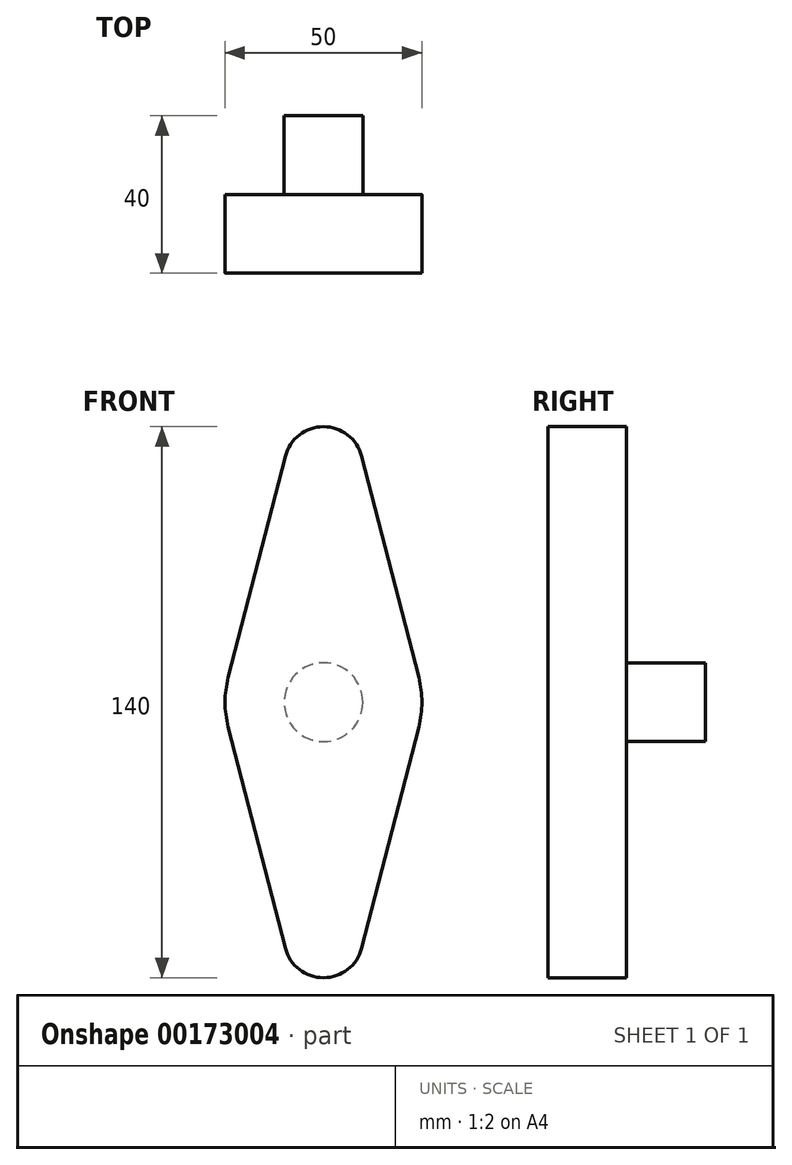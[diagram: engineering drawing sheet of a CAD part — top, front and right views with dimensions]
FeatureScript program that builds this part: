
annotation { "Feature Type Name" : "Feature", "Feature Type Description" : "" }
export const myFeature = defineFeature(function(context is Context, id is Id, definition is map)
    precondition{}
    {
        {
            var Q0;
            Q0=qCreatedBy(makeId("Front.planeOp"),FACE);
            var sketch = newSketch(context, id + "F0", { "sketchPlane" : qUnion([Q0])});
            skCircle(sketch, "E0", {"center": v(0, 0) * mm, "radius": 25 * mm});
            skCircle(sketch, "E1", {"center": v(0, 60) * mm, "radius": 10 * mm});
            skCircle(sketch, "E2", {"center": v(0, -60) * mm, "radius": 10 * mm});
            skLineSegment(sketch, "E3", {"start": v(0, 0) * mm, "end": v(0, 60) * mm, "construction": true});
            skLineSegment(sketch, "E4", {"start": v(0, 0) * mm, "end": v(0, -60) * mm, "construction": true});
            skLineSegment(sketch, "E5", {"start": v(-9.68, 62.5) * mm, "end": v(-24.2, 6.25) * mm});
            skLineSegment(sketch, "E6.MirrorCS", {"start": v(9.68, 62.5) * mm, "end": v(24.2, 6.25) * mm});
            skLineSegment(sketch, "E7", {"start": v(-24.2, -6.25) * mm, "end": v(-9.68, -62.5) * mm});
            skLineSegment(sketch, "E8.MirrorCS", {"start": v(24.2, -6.25) * mm, "end": v(9.68, -62.5) * mm});
            skSolve(sketch);
        }
        {
            var Q0;
            Q0 = qSketchRegion(id + "F0", true);
            extrude(context, id + "F1", {"entities" : qUnion([Q0]), "depth" : 20 * mm});
        }
        {
            var Q0;
            Q0=makeQuery(id+"F1.opExtrude","CAP_FACE",FACE,{"disambiguationData":[OSD([sQuery(id+"F0.wireOp",EDGE,"E0"),sQuery(id+"F0.wireOp",EDGE,"E1"),sQuery(id+"F0.wireOp",EDGE,"E2"),sQuery(id+"F0.wireOp",EDGE,"E5"),sQuery(id+"F0.wireOp",EDGE,"E6.MirrorCS"),sQuery(id+"F0.wireOp",EDGE,"E7"),sQuery(id+"F0.wireOp",EDGE,"E8.MirrorCS")])],"isStart":true});
            var sketch = newSketch(context, id + "F2", { "sketchPlane" : qUnion([Q0])});
            skCircle(sketch, "E9", {"center": v(0, 0) * mm, "radius": 10 * mm});
            skSolve(sketch);
        }
        {
            var Q0;
            Q0 = qSketchRegion(id + "F2", true);
            extrude(context, id + "F3", {"entities" : qUnion([Q0]), "operationType" : NewBodyOperationType.ADD, "depth" : 20 * mm});
        }
    });
